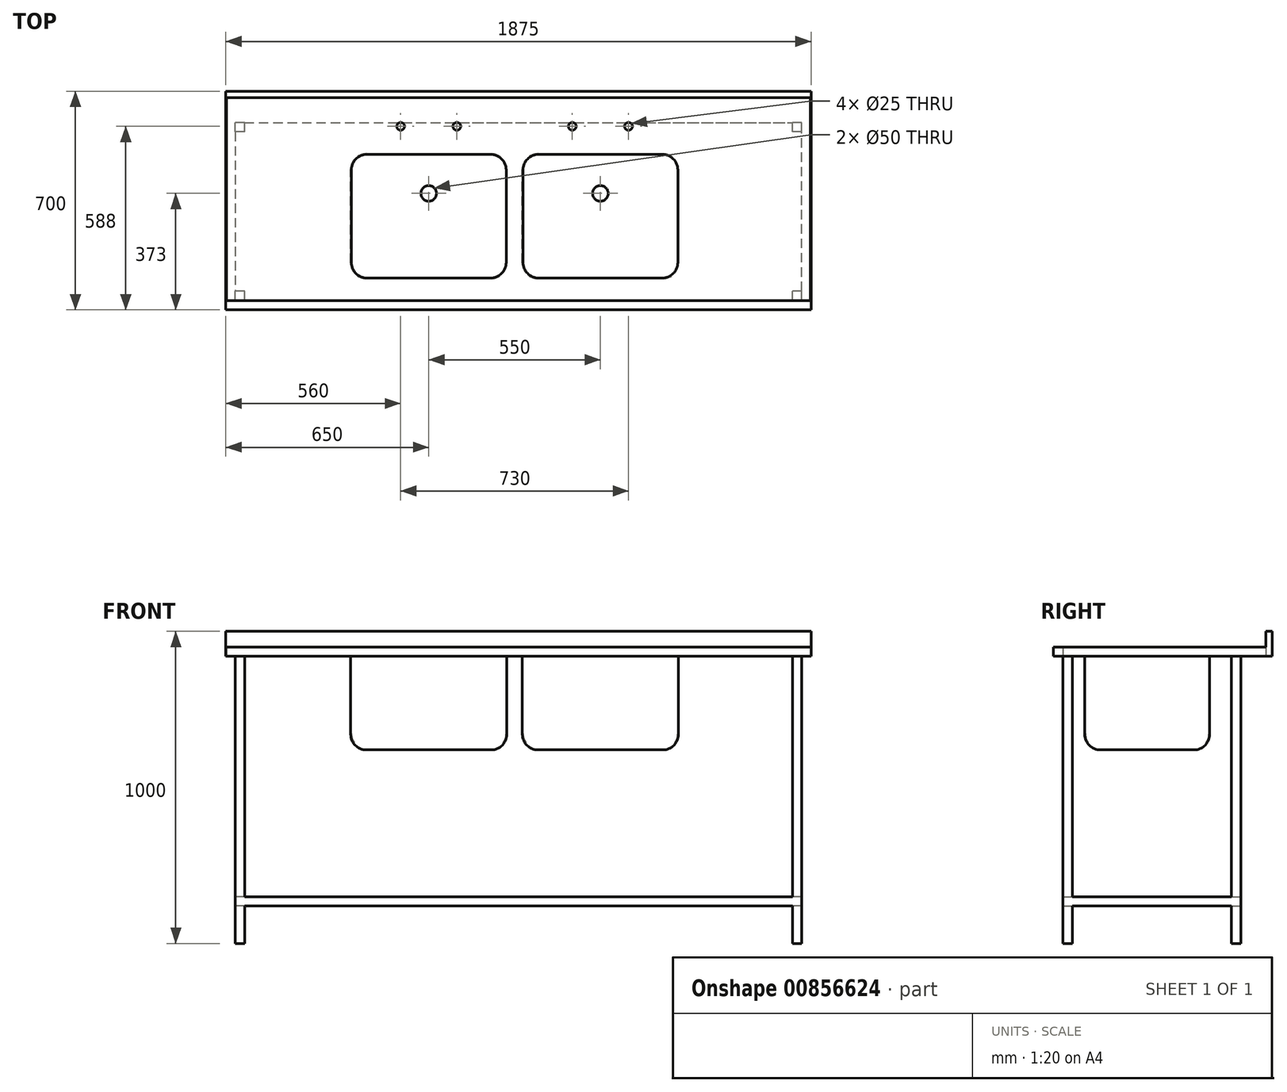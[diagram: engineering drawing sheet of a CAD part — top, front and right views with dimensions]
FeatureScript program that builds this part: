
annotation { "Feature Type Name" : "Feature", "Feature Type Description" : "" }
export const myFeature = defineFeature(function(context is Context, id is Id, definition is map)
    precondition{}
    {
        {
            var Q0;
            Q0=qCreatedBy(makeId("Right.planeOp"),FACE);
            var sketch = newSketch(context, id + "F0", { "sketchPlane" : qUnion([Q0])});
            skLineSegment(sketch, "E0", {"start": v(0, 0) * mm, "end": v(700, 0) * mm});
            skLineSegment(sketch, "E1", {"start": v(700, 0) * mm, "end": v(700, 80) * mm});
            skLineSegment(sketch, "E2", {"start": v(700, 80) * mm, "end": v(680, 80) * mm});
            skLineSegment(sketch, "E3", {"start": v(0, 0) * mm, "end": v(0, 30) * mm});
            skLineSegment(sketch, "E4", {"start": v(0, 30) * mm, "end": v(30, 30) * mm});
            skLineSegment(sketch, "E5", {"start": v(30, 30) * mm, "end": v(30, 2) * mm});
            skLineSegment(sketch, "E6", {"start": v(30, 2) * mm, "end": v(680, 2) * mm});
            skLineSegment(sketch, "E7", {"start": v(680, 80) * mm, "end": v(680, 2) * mm});
            skSolve(sketch);
        }
        {
            var Q0;
            Q0 = qSketchRegion(id + "F0", true);
            extrude(context, id + "F1", {"entities" : qUnion([Q0]), "depth" : 1875 * mm, "offsetDistance" : 25 * mm});
        }
        {
            var Q0;
            Q0=makeQuery(id+"F1.opExtrude","SWEPT_FACE",FACE,{"disambiguationData":[OSD([sQuery(id+"F0.wireOp",EDGE,"E5")])]});
            var sketch = newSketch(context, id + "F2", { "sketchPlane" : qUnion([Q0])});
            skLineSegment(sketch, "E8.bottom", {"start": v(-1875, 30) * mm, "end": v(-1873, 30) * mm});
            skLineSegment(sketch, "E8.top", {"start": v(-1875, 2) * mm, "end": v(-1873, 2) * mm});
            skLineSegment(sketch, "E8.left", {"start": v(-1875, 30) * mm, "end": v(-1875, 2) * mm});
            skLineSegment(sketch, "E8.right", {"start": v(-1873, 30) * mm, "end": v(-1873, 2) * mm});
            skLineSegment(sketch, "E9.bottom", {"start": v(0, 30) * mm, "end": v(-2, 30) * mm});
            skLineSegment(sketch, "E9.top", {"start": v(0, 2) * mm, "end": v(-2, 2) * mm});
            skLineSegment(sketch, "E9.left", {"start": v(0, 30) * mm, "end": v(0, 2) * mm});
            skLineSegment(sketch, "E9.right", {"start": v(-2, 30) * mm, "end": v(-2, 2) * mm});
            skSolve(sketch);
        }
        {
            var Q0;
            Q0 = qSketchRegion(id + "F2", true);
            extrude(context, id + "F3", {"entities" : qUnion([Q0]), "operationType" : NewBodyOperationType.ADD, "endBound" : BoundingType.UP_TO_NEXT, "depth" : 25 * mm, "offsetDistance" : 25 * mm});
        }
        {
            var Q0;
            Q0=makeQuery(id+"F1.opExtrude","SWEPT_FACE",FACE,{"disambiguationData":[OSD([sQuery(id+"F0.wireOp",EDGE,"E0")])]});
            var sketch = newSketch(context, id + "F4", { "sketchPlane" : qUnion([Q0])});
            skLineSegment(sketch, "E10.bottom", {"start": v(400, -100) * mm, "end": v(900, -100) * mm});
            skLineSegment(sketch, "E10.top", {"start": v(400, -500) * mm, "end": v(900, -500) * mm});
            skLineSegment(sketch, "E10.left", {"start": v(400, -100) * mm, "end": v(400, -500) * mm});
            skLineSegment(sketch, "E10.right", {"start": v(900, -100) * mm, "end": v(900, -500) * mm});
            skLineSegment(sketch, "E11.bottom", {"start": v(950, -100) * mm, "end": v(1450, -100) * mm});
            skLineSegment(sketch, "E11.top", {"start": v(950, -500) * mm, "end": v(1450, -500) * mm});
            skLineSegment(sketch, "E11.left", {"start": v(950, -100) * mm, "end": v(950, -500) * mm});
            skLineSegment(sketch, "E11.right", {"start": v(1450, -100) * mm, "end": v(1450, -500) * mm});
            skSolve(sketch);
        }
        {
            var Q0;
            Q0 = qSketchRegion(id + "F4", true);
            extrude(context, id + "F5", {"entities" : qUnion([Q0]), "operationType" : NewBodyOperationType.ADD, "depth" : 300 * mm, "offsetDistance" : 25 * mm});
        }
        {
            var Q0;
            Q0=makeQuery(id+"F1.opExtrude","SWEPT_FACE",FACE,{"disambiguationData":[OSD([sQuery(id+"F0.wireOp",EDGE,"E6")])]});
            var sketch = newSketch(context, id + "F6", { "sketchPlane" : qUnion([Q0])});
            skLineSegment(sketch, "E12.bottom", {"start": v(402, 498) * mm, "end": v(898, 498) * mm});
            skLineSegment(sketch, "E12.top", {"start": v(402, 102) * mm, "end": v(898, 102) * mm});
            skLineSegment(sketch, "E12.left", {"start": v(402, 498) * mm, "end": v(402, 102) * mm});
            skLineSegment(sketch, "E12.right", {"start": v(898, 498) * mm, "end": v(898, 102) * mm});
            skLineSegment(sketch, "E13.bottom", {"start": v(952, 498) * mm, "end": v(1448, 498) * mm});
            skLineSegment(sketch, "E13.top", {"start": v(952, 102) * mm, "end": v(1448, 102) * mm});
            skLineSegment(sketch, "E13.left", {"start": v(952, 498) * mm, "end": v(952, 102) * mm});
            skLineSegment(sketch, "E13.right", {"start": v(1448, 498) * mm, "end": v(1448, 102) * mm});
            skSolve(sketch);
        }
        {
            var Q0;
            Q0 = qSketchRegion(id + "F6", true);
            extrude(context, id + "F7", {"entities" : qUnion([Q0]), "operationType" : NewBodyOperationType.REMOVE, "oppositeDirection" : true, "depth" : 300 * mm, "offsetDistance" : 25 * mm});
        }
        {
            var Q0;
            Q0=makeQuery(id+"F7.boolean.opBoolean","COPY",EDGE,{"derivedFrom":makeQuery(id+"F7.opExtrude","SWEPT_EDGE",EDGE,{"disambiguationData":[OSD([sQuery(id+"F6.wireOp",EDGE,"E12.top"),sQuery(id+"F6.wireOp",EDGE,"E12.left")])]})});
            var Q1;
            Q1=makeQuery(id+"F7.boolean.opBoolean","COPY",EDGE,{"derivedFrom":makeQuery(id+"F7.opExtrude","SWEPT_EDGE",EDGE,{"disambiguationData":[OSD([sQuery(id+"F6.wireOp",EDGE,"E12.bottom"),sQuery(id+"F6.wireOp",EDGE,"E12.left")])]})});
            var Q2;
            Q2=makeQuery(id+"F7.boolean.opBoolean","COPY",EDGE,{"derivedFrom":makeQuery(id+"F7.opExtrude","SWEPT_EDGE",EDGE,{"disambiguationData":[OSD([sQuery(id+"F6.wireOp",EDGE,"E13.bottom"),sQuery(id+"F6.wireOp",EDGE,"E13.left")])]})});
            var Q3;
            Q3=makeQuery(id+"F7.boolean.opBoolean","COPY",EDGE,{"derivedFrom":makeQuery(id+"F7.opExtrude","SWEPT_EDGE",EDGE,{"disambiguationData":[OSD([sQuery(id+"F6.wireOp",EDGE,"E13.bottom"),sQuery(id+"F6.wireOp",EDGE,"E13.right")])]})});
            var Q4;
            Q4=makeQuery(id+"F7.boolean.opBoolean","COPY",EDGE,{"derivedFrom":makeQuery(id+"F7.opExtrude","SWEPT_EDGE",EDGE,{"disambiguationData":[OSD([sQuery(id+"F6.wireOp",EDGE,"E12.bottom"),sQuery(id+"F6.wireOp",EDGE,"E12.right")])]})});
            var Q5;
            Q5=makeQuery(id+"F7.boolean.opBoolean","COPY",EDGE,{"derivedFrom":makeQuery(id+"F7.opExtrude","SWEPT_EDGE",EDGE,{"disambiguationData":[OSD([sQuery(id+"F6.wireOp",EDGE,"E12.top"),sQuery(id+"F6.wireOp",EDGE,"E12.right")])]})});
            var Q6;
            Q6=makeQuery(id+"F7.boolean.opBoolean","COPY",EDGE,{"derivedFrom":makeQuery(id+"F7.opExtrude","SWEPT_EDGE",EDGE,{"disambiguationData":[OSD([sQuery(id+"F6.wireOp",EDGE,"E13.top"),sQuery(id+"F6.wireOp",EDGE,"E13.right")])]})});
            var Q7;
            Q7=makeQuery(id+"F7.boolean.opBoolean","COPY",EDGE,{"derivedFrom":makeQuery(id+"F7.opExtrude","CAP_EDGE",EDGE,{"disambiguationData":[OSD([sQuery(id+"F6.wireOp",EDGE,"E13.right")])],"isStart":false})});
            var Q8;
            Q8=makeQuery(id+"F7.boolean.opBoolean","COPY",EDGE,{"derivedFrom":makeQuery(id+"F7.opExtrude","CAP_EDGE",EDGE,{"disambiguationData":[OSD([sQuery(id+"F6.wireOp",EDGE,"E13.bottom")])],"isStart":false})});
            var Q9;
            Q9=makeQuery(id+"F7.boolean.opBoolean","COPY",EDGE,{"derivedFrom":makeQuery(id+"F7.opExtrude","CAP_EDGE",EDGE,{"disambiguationData":[OSD([sQuery(id+"F6.wireOp",EDGE,"E13.left")])],"isStart":false})});
            var Q10;
            Q10=makeQuery(id+"F7.boolean.opBoolean","COPY",EDGE,{"derivedFrom":makeQuery(id+"F7.opExtrude","SWEPT_EDGE",EDGE,{"disambiguationData":[OSD([sQuery(id+"F6.wireOp",EDGE,"E13.top"),sQuery(id+"F6.wireOp",EDGE,"E13.left")])]})});
            var Q11;
            Q11=makeQuery(id+"F7.boolean.opBoolean","COPY",EDGE,{"derivedFrom":makeQuery(id+"F7.opExtrude","CAP_EDGE",EDGE,{"disambiguationData":[OSD([sQuery(id+"F6.wireOp",EDGE,"E13.top")])],"isStart":false})});
            var Q12;
            Q12=makeQuery(id+"F7.boolean.opBoolean","COPY",EDGE,{"derivedFrom":makeQuery(id+"F7.opExtrude","CAP_EDGE",EDGE,{"disambiguationData":[OSD([sQuery(id+"F6.wireOp",EDGE,"E12.top")])],"isStart":false})});
            var Q13;
            Q13=makeQuery(id+"F7.boolean.opBoolean","COPY",EDGE,{"derivedFrom":makeQuery(id+"F7.opExtrude","CAP_EDGE",EDGE,{"disambiguationData":[OSD([sQuery(id+"F6.wireOp",EDGE,"E12.left")])],"isStart":false})});
            var Q14;
            Q14=makeQuery(id+"F7.boolean.opBoolean","COPY",EDGE,{"derivedFrom":makeQuery(id+"F7.opExtrude","CAP_EDGE",EDGE,{"disambiguationData":[OSD([sQuery(id+"F6.wireOp",EDGE,"E12.bottom")])],"isStart":false})});
            var Q15;
            Q15=makeQuery(id+"F7.boolean.opBoolean","COPY",EDGE,{"derivedFrom":makeQuery(id+"F7.opExtrude","CAP_EDGE",EDGE,{"disambiguationData":[OSD([sQuery(id+"F6.wireOp",EDGE,"E12.right")])],"isStart":false})});
            fillet(context, id + "F8", {"entities" : qUnion([Q0, Q1, Q2, Q3, Q4, Q5, Q6, Q7, Q8, Q9, Q10, Q11, Q12, Q13, Q14, Q15]), "radius" : 50 * mm, "tangentPropagation" : true, "allowEdgeOverflow" : false});
        }
        {
            var Q0;
            Q0=makeQuery(id+"F5.opExtrude","SWEPT_EDGE",EDGE,{"disambiguationData":[OSD([sQuery(id+"F4.wireOp",EDGE,"E10.bottom"),sQuery(id+"F4.wireOp",EDGE,"E10.left")])]});
            var Q1;
            Q1=makeQuery(id+"F5.opExtrude","SWEPT_EDGE",EDGE,{"disambiguationData":[OSD([sQuery(id+"F4.wireOp",EDGE,"E10.bottom"),sQuery(id+"F4.wireOp",EDGE,"E10.right")])]});
            var Q2;
            Q2=makeQuery(id+"F5.opExtrude","SWEPT_EDGE",EDGE,{"disambiguationData":[OSD([sQuery(id+"F4.wireOp",EDGE,"E11.bottom"),sQuery(id+"F4.wireOp",EDGE,"E11.left")])]});
            var Q3;
            Q3=makeQuery(id+"F5.opExtrude","SWEPT_EDGE",EDGE,{"disambiguationData":[OSD([sQuery(id+"F4.wireOp",EDGE,"E11.bottom"),sQuery(id+"F4.wireOp",EDGE,"E11.right")])]});
            var Q4;
            Q4=makeQuery(id+"F5.opExtrude","SWEPT_EDGE",EDGE,{"disambiguationData":[OSD([sQuery(id+"F4.wireOp",EDGE,"E11.top"),sQuery(id+"F4.wireOp",EDGE,"E11.right")])]});
            var Q5;
            Q5=makeQuery(id+"F5.opExtrude","SWEPT_EDGE",EDGE,{"disambiguationData":[OSD([sQuery(id+"F4.wireOp",EDGE,"E11.top"),sQuery(id+"F4.wireOp",EDGE,"E11.left")])]});
            var Q6;
            Q6=makeQuery(id+"F5.opExtrude","SWEPT_EDGE",EDGE,{"disambiguationData":[OSD([sQuery(id+"F4.wireOp",EDGE,"E10.top"),sQuery(id+"F4.wireOp",EDGE,"E10.right")])]});
            var Q7;
            Q7=makeQuery(id+"F5.opExtrude","SWEPT_EDGE",EDGE,{"disambiguationData":[OSD([sQuery(id+"F4.wireOp",EDGE,"E10.top"),sQuery(id+"F4.wireOp",EDGE,"E10.left")])]});
            var Q8;
            Q8=makeQuery(id+"F5.opExtrude","CAP_EDGE",EDGE,{"disambiguationData":[OSD([sQuery(id+"F4.wireOp",EDGE,"E10.left")])],"isStart":false});
            var Q9;
            Q9=makeQuery(id+"F5.opExtrude","CAP_EDGE",EDGE,{"disambiguationData":[OSD([sQuery(id+"F4.wireOp",EDGE,"E10.top")])],"isStart":false});
            var Q10;
            Q10=makeQuery(id+"F5.opExtrude","CAP_EDGE",EDGE,{"disambiguationData":[OSD([sQuery(id+"F4.wireOp",EDGE,"E10.right")])],"isStart":false});
            var Q11;
            Q11=makeQuery(id+"F5.opExtrude","CAP_EDGE",EDGE,{"disambiguationData":[OSD([sQuery(id+"F4.wireOp",EDGE,"E10.bottom")])],"isStart":false});
            var Q12;
            Q12=makeQuery(id+"F5.opExtrude","CAP_EDGE",EDGE,{"disambiguationData":[OSD([sQuery(id+"F4.wireOp",EDGE,"E11.left")])],"isStart":false});
            var Q13;
            Q13=makeQuery(id+"F5.opExtrude","CAP_EDGE",EDGE,{"disambiguationData":[OSD([sQuery(id+"F4.wireOp",EDGE,"E11.top")])],"isStart":false});
            var Q14;
            Q14=makeQuery(id+"F5.opExtrude","CAP_EDGE",EDGE,{"disambiguationData":[OSD([sQuery(id+"F4.wireOp",EDGE,"E11.right")])],"isStart":false});
            var Q15;
            Q15=makeQuery(id+"F5.opExtrude","CAP_EDGE",EDGE,{"disambiguationData":[OSD([sQuery(id+"F4.wireOp",EDGE,"E11.bottom")])],"isStart":false});
            fillet(context, id + "F9", {"entities" : qUnion([Q0, Q1, Q2, Q3, Q4, Q5, Q6, Q7, Q8, Q9, Q10, Q11, Q12, Q13, Q14, Q15]), "radius" : 50 * mm, "tangentPropagation" : true, "allowEdgeOverflow" : false});
        }
        {
            var Q0;
            Q0=makeQuery(id+"F7.boolean.opBoolean","COPY",FACE,{"derivedFrom":makeQuery(id+"F7.opExtrude","CAP_FACE",FACE,{"disambiguationData":[OSD([sQuery(id+"F6.wireOp",EDGE,"E12.bottom"),sQuery(id+"F6.wireOp",EDGE,"E12.top"),sQuery(id+"F6.wireOp",EDGE,"E12.left"),sQuery(id+"F6.wireOp",EDGE,"E12.right")])],"isStart":false})});
            var sketch = newSketch(context, id + "F10", { "sketchPlane" : qUnion([Q0])});
            skCircle(sketch, "E14", {"center": v(650, 373) * mm, "radius": 25 * mm});
            skPoint(sketch, "E14.centerSnap0", {"position": v(650, 448) * mm});
            skCircle(sketch, "E15", {"center": v(1200, 373) * mm, "radius": 25 * mm});
            skSolve(sketch);
        }
        {
            var Q0;
            Q0 = qSketchRegion(id + "F10", true);
            extrude(context, id + "F11", {"entities" : qUnion([Q0]), "operationType" : NewBodyOperationType.REMOVE, "endBound" : BoundingType.UP_TO_NEXT, "oppositeDirection" : true, "depth" : 25 * mm, "offsetDistance" : 25 * mm});
        }
        {
            var Q0;
            Q0=makeQuery(id+"F1.opExtrude","SWEPT_FACE",FACE,{"disambiguationData":[OSD([sQuery(id+"F0.wireOp",EDGE,"E6")])]});
            var sketch = newSketch(context, id + "F12", { "sketchPlane" : qUnion([Q0])});
            skCircle(sketch, "E16", {"center": v(560, 588) * mm, "radius": 12.5 * mm});
            skCircle(sketch, "E17", {"center": v(740, 588) * mm, "radius": 12.5 * mm});
            skCircle(sketch, "E18", {"center": v(1110, 588) * mm, "radius": 12.5 * mm});
            skCircle(sketch, "E19", {"center": v(1290, 588) * mm, "radius": 12.5 * mm});
            skSolve(sketch);
        }
        {
            var Q0;
            Q0 = qSketchRegion(id + "F12", true);
            extrude(context, id + "F13", {"entities" : qUnion([Q0]), "operationType" : NewBodyOperationType.REMOVE, "endBound" : BoundingType.UP_TO_NEXT, "oppositeDirection" : true, "depth" : 25 * mm, "offsetDistance" : 25 * mm});
        }
        {
            var Q0;
            Q0=makeQuery(id+"F1.opExtrude","SWEPT_FACE",FACE,{"disambiguationData":[OSD([sQuery(id+"F0.wireOp",EDGE,"E0")])]});
            var sketch = newSketch(context, id + "F14", { "sketchPlane" : qUnion([Q0])});
            skLineSegment(sketch, "E20.bottom", {"start": v(60, -30) * mm, "end": v(30, -30) * mm});
            skLineSegment(sketch, "E20.top", {"start": v(60, -60) * mm, "end": v(30, -60) * mm});
            skLineSegment(sketch, "E20.left", {"start": v(60, -30) * mm, "end": v(60, -60) * mm});
            skLineSegment(sketch, "E20.right", {"start": v(30, -30) * mm, "end": v(30, -60) * mm});
            skPoint(sketch, "E20.middle", {"position": v(45, -45) * mm});
            skLineSegment(sketch, "E21.bottom", {"start": v(1845, -30) * mm, "end": v(1815, -30) * mm});
            skLineSegment(sketch, "E21.top", {"start": v(1845, -60) * mm, "end": v(1815, -60) * mm});
            skLineSegment(sketch, "E21.left", {"start": v(1845, -30) * mm, "end": v(1845, -60) * mm});
            skLineSegment(sketch, "E21.right", {"start": v(1815, -30) * mm, "end": v(1815, -60) * mm});
            skPoint(sketch, "E21.middle", {"position": v(1830, -45) * mm});
            skLineSegment(sketch, "E22.bottom", {"start": v(1845, -570) * mm, "end": v(1815, -570) * mm});
            skLineSegment(sketch, "E22.top", {"start": v(1845, -600) * mm, "end": v(1815, -600) * mm});
            skLineSegment(sketch, "E22.left", {"start": v(1845, -570) * mm, "end": v(1845, -600) * mm});
            skLineSegment(sketch, "E22.right", {"start": v(1815, -570) * mm, "end": v(1815, -600) * mm});
            skPoint(sketch, "E22.middle", {"position": v(1830, -585) * mm});
            skLineSegment(sketch, "E23.bottom", {"start": v(60, -570) * mm, "end": v(30, -570) * mm});
            skLineSegment(sketch, "E23.top", {"start": v(60, -600) * mm, "end": v(30, -600) * mm});
            skLineSegment(sketch, "E23.left", {"start": v(60, -570) * mm, "end": v(60, -600) * mm});
            skLineSegment(sketch, "E23.right", {"start": v(30, -570) * mm, "end": v(30, -600) * mm});
            skPoint(sketch, "E23.middle", {"position": v(45, -585) * mm});
            skPoint(sketch, "E23.middle.positionSnap0", {"position": v(45, -60) * mm});
            skPoint(sketch, "E23.cornerSnap0", {"position": v(1830, -570) * mm});
            skPoint(sketch, "E23.centerSnap0", {"position": v(45, -60) * mm});
            skSolve(sketch);
        }
        {
            var Q0;
            Q0 = qSketchRegion(id + "F14", true);
            extrude(context, id + "F15", {"entities" : qUnion([Q0]), "operationType" : NewBodyOperationType.ADD, "depth" : 920 * mm, "offsetDistance" : 25 * mm});
        }
        {
            var Q0;
            Q0=makeQuery(id+"F15.opExtrude","SWEPT_FACE",FACE,{"disambiguationData":[OSD([sQuery(id+"F14.wireOp",EDGE,"E21.left")])]});
            var sketch = newSketch(context, id + "F16", { "sketchPlane" : qUnion([Q0])});
            skLineSegment(sketch, "E24.bottom", {"start": v(30, -770) * mm, "end": v(600, -770) * mm});
            skLineSegment(sketch, "E24.top", {"start": v(30, -800) * mm, "end": v(600, -800) * mm});
            skLineSegment(sketch, "E24.left", {"start": v(30, -770) * mm, "end": v(30, -800) * mm});
            skLineSegment(sketch, "E24.right", {"start": v(600, -770) * mm, "end": v(600, -800) * mm});
            skSolve(sketch);
        }
        {
            var Q0;
            Q0 = qSketchRegion(id + "F16", true);
            var Q1;
            Q1=makeQuery(id+"F15.opExtrude","SWEPT_FACE",FACE,{"disambiguationData":[OSD([sQuery(id+"F14.wireOp",EDGE,"E20.right")])]});
            extrude(context, id + "F17", {"entities" : qUnion([Q0]), "operationType" : NewBodyOperationType.ADD, "endBound" : BoundingType.UP_TO_SURFACE, "oppositeDirection" : true, "depth" : 25 * mm, "endBoundEntityFace" : qUnion([Q1]), "offsetDistance" : 25 * mm});
        }
    });
